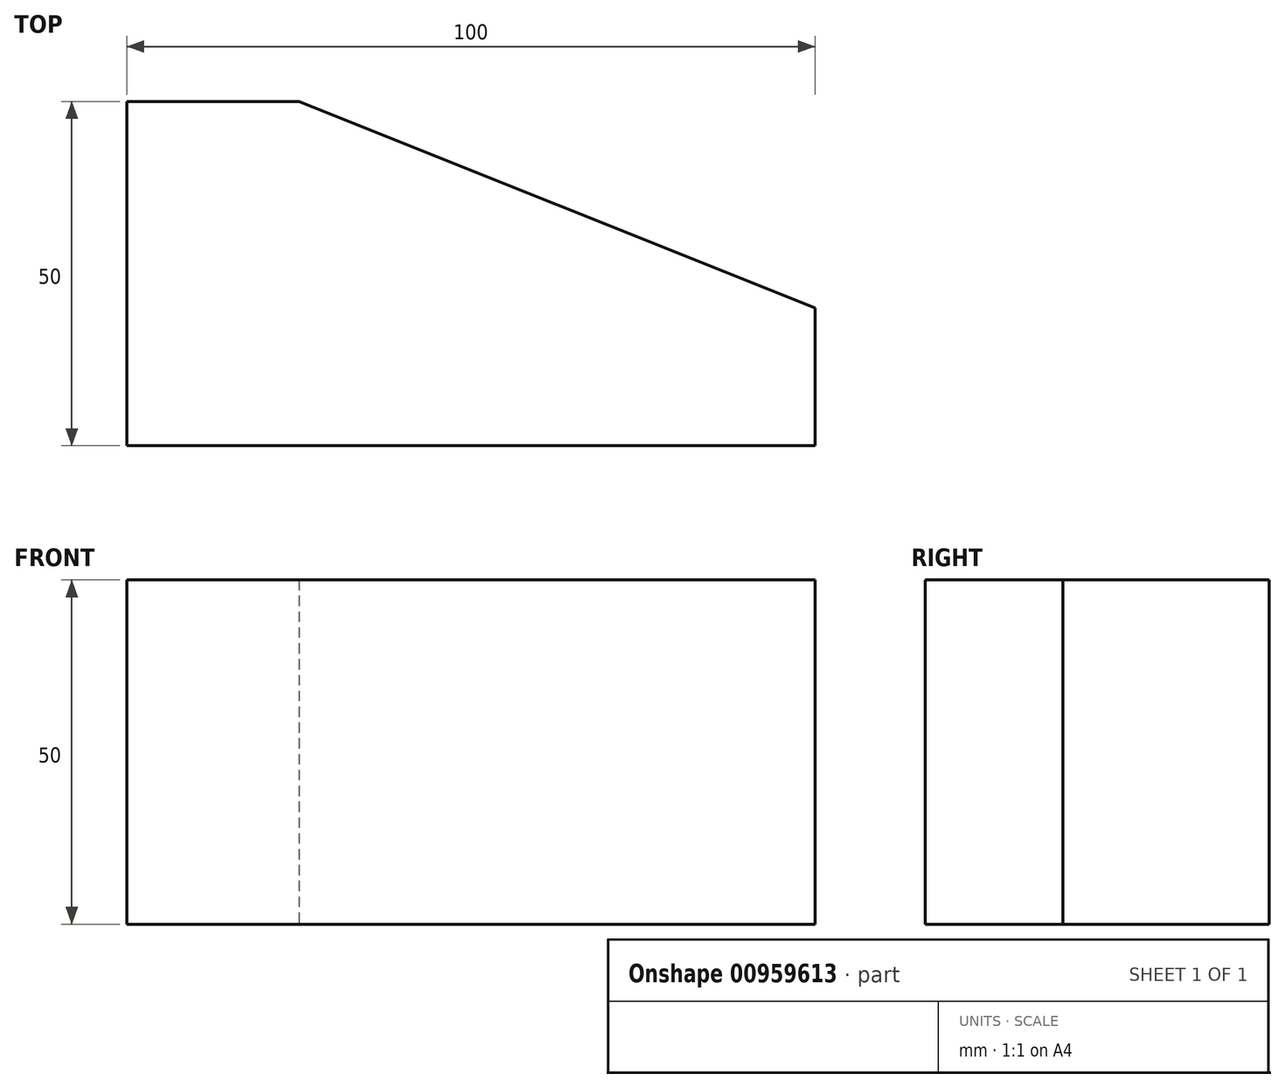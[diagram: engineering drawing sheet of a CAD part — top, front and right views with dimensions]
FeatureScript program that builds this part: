
annotation { "Feature Type Name" : "Feature", "Feature Type Description" : "" }
export const myFeature = defineFeature(function(context is Context, id is Id, definition is map)
    precondition{}
    {
        {
            var Q0;
            Q0=qCreatedBy(makeId("Top.planeOp"),FACE);
            var sketch = newSketch(context, id + "F0", { "sketchPlane" : qUnion([Q0])});
            skLineSegment(sketch, "E0", {"start": v(0, 0) * mm, "end": v(100, 0) * mm});
            skLineSegment(sketch, "E1", {"start": v(100, 0) * mm, "end": v(100, 20) * mm});
            skLineSegment(sketch, "E2", {"start": v(100, 20) * mm, "end": v(25, 50) * mm});
            skLineSegment(sketch, "E3", {"start": v(25, 50) * mm, "end": v(0, 50) * mm});
            skLineSegment(sketch, "E4", {"start": v(0, 50) * mm, "end": v(0, 0) * mm});
            skSolve(sketch);
        }
        {
            var Q0;
            Q0=makeQuery(id+"F0.imprint","IMPRINT",FACE,{"disambiguationData":[TD([[makeQuery(id+"F0.imprint","IMPRINT",EDGE,{"derivedFrom":sQuery(id+"F0.wireOp",EDGE,"E0")}),1.0]])]});
            extrude(context, id + "F1", {"entities" : qUnion([Q0]), "depth" : 50 * mm, "offsetDistance" : 25 * mm});
        }
    });
